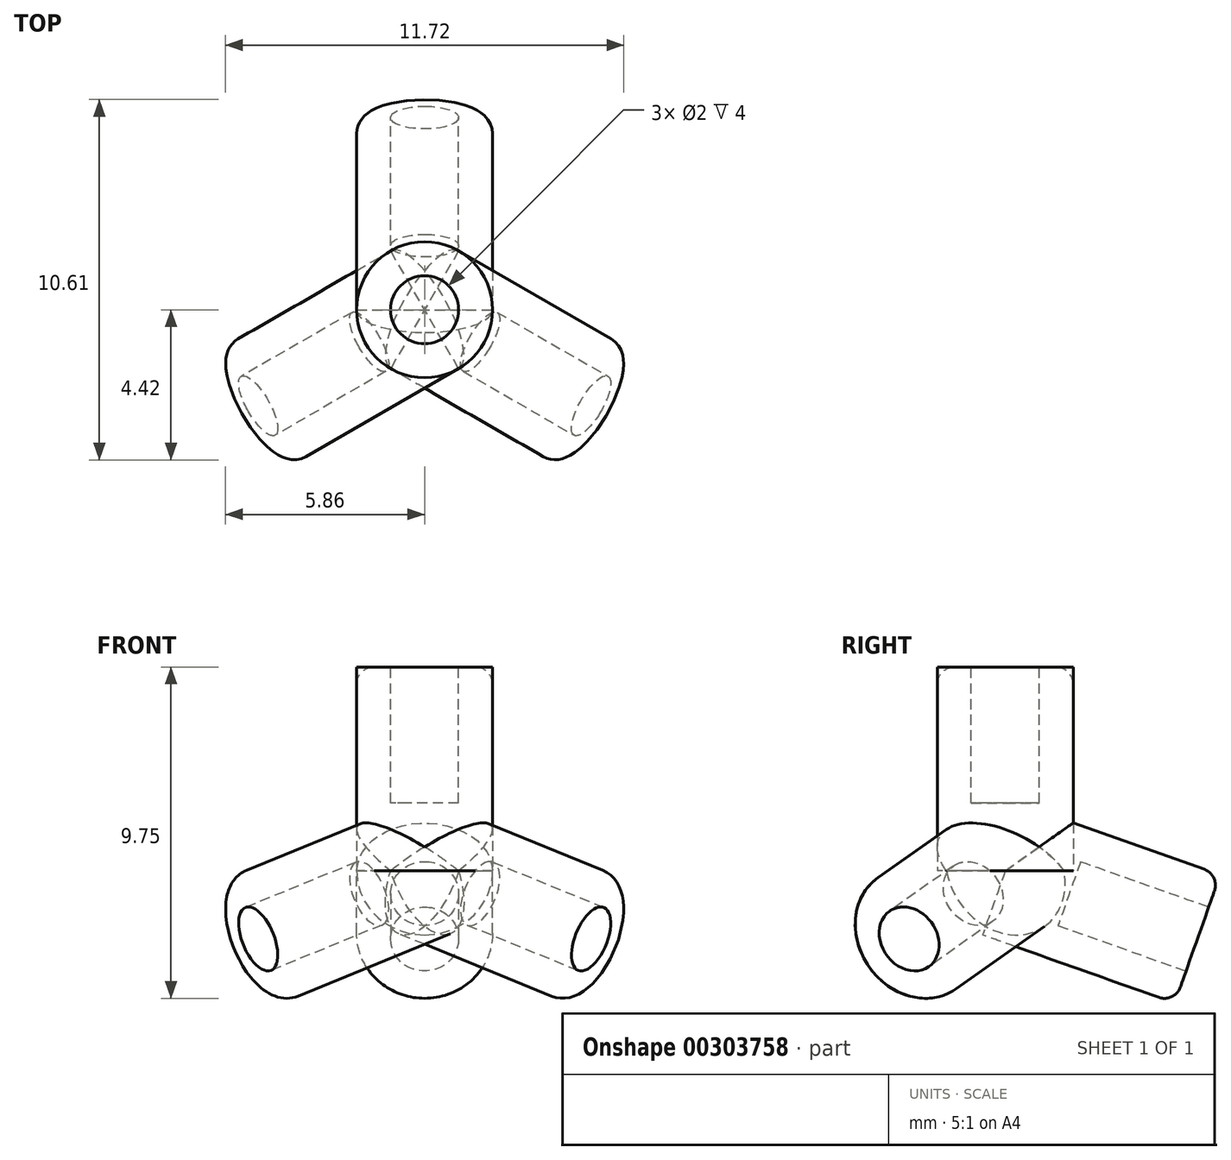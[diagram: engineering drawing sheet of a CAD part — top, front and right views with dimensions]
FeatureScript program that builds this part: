
annotation { "Feature Type Name" : "Feature", "Feature Type Description" : "" }
export const myFeature = defineFeature(function(context is Context, id is Id, definition is map)
    precondition{}
    {
        {
            var Q0;
            Q0=qCreatedBy(makeId("Top.planeOp"),FACE);
            var sketch = newSketch(context, id + "F0", { "sketchPlane" : qUnion([Q0])});
            skCircle(sketch, "E0", {"center": v(0, 0) * mm, "radius": 2 * mm});
            skSolve(sketch);
        }
        {
            var Q0;
            Q0=makeQuery(id+"F0.imprint","IMPRINT",FACE,{"disambiguationData":[TD([[makeQuery(id+"F0.imprint","IMPRINT",EDGE,{"derivedFrom":sQuery(id+"F0.wireOp",EDGE,"E0")}),1.0]])]});
            extrude(context, id + "F1", {"entities" : qUnion([Q0]), "flatOperationType" : FlatOperationType.REMOVE, "offsetDistance" : 25 * mm, "depth" : 6 * mm, "domain" : OperationDomain.MODEL});
        }
        {
            var Q0;
            Q0=qCreatedBy(makeId("Top.planeOp"),FACE);
            var sketch = newSketch(context, id + "F2", { "sketchPlane" : qUnion([Q0])});
            skLineSegment(sketch, "E1", {"start": v(74.45, 0) * mm, "end": v(-75.52, 0) * mm, "construction": true});
            skSolve(sketch);
        }
        {
            var Q0;
            Q0=sQuery(id+"F2.wireOp",EDGE,"E1");
            var Q1;
            Q1=qCreatedBy(makeId("Top.planeOp"),FACE);
            cPlane(context, id + "F3", {"entities" : qUnion([Q0, Q1]), "cplaneType" : CPlaneType.LINE_ANGLE, "offset" : 25 * mm, "angle" : 109.5 * degree, "width" : 150 * mm, "height" : 150 * mm});
        }
        {
            var Q0;
            Q0=qCreatedBy(id+"F3.planeOp",FACE);
            var sketch = newSketch(context, id + "F4", { "sketchPlane" : qUnion([Q0])});
            skCircle(sketch, "E2", {"center": v(0, 0) * mm, "radius": 2 * mm});
            skSolve(sketch);
        }
        {
            var Q0;
            Q0 = qSketchRegion(id + "F4", true);
            extrude(context, id + "F5", {"entities" : qUnion([Q0]), "operationType" : NewBodyOperationType.ADD, "oppositeDirection" : true, "depth" : 6 * mm});
        }
        {
            var Q0;
            Q0=makeQuery(id+"F1.opExtrude","CAP_FACE",FACE,{"disambiguationData":[OSD([sQuery(id+"F0.wireOp",EDGE,"E0")])],"isStart":false});
            var sketch = newSketch(context, id + "F6", { "sketchPlane" : qUnion([Q0])});
            skCircle(sketch, "E3", {"center": v(0, 0) * mm, "radius": 1 * mm});
            skSolve(sketch);
        }
        {
            var Q0;
            Q0=qCreatedBy(makeId("Front.planeOp"),FACE);
            var sketch = newSketch(context, id + "F7", { "sketchPlane" : qUnion([Q0])});
            skLineSegment(sketch, "E4", {"start": v(0, 0) * mm, "end": v(0, 47.07) * mm, "construction": true});
            skSolve(sketch);
        }
        {
            var Q0;
            Q0=makeQuery(id+"F5.opExtrude","CAP_FACE",FACE,{"disambiguationData":[OSD([sQuery(id+"F4.wireOp",EDGE,"E2")])],"isStart":false});
            var sketch = newSketch(context, id + "F8", { "sketchPlane" : qUnion([Q0])});
            skCircle(sketch, "E5", {"center": v(0, 0) * mm, "radius": 1 * mm});
            skSolve(sketch);
        }
        {
            var Q0;
            Q0 = qSketchRegion(id + "F6", true);
            extrude(context, id + "F9", {"entities" : qUnion([Q0]), "operationType" : NewBodyOperationType.REMOVE, "oppositeDirection" : true, "depth" : 4 * mm});
        }
        {
            var Q0;
            Q0=makeQuery(id+"F8.imprint","IMPRINT",FACE,{"disambiguationData":[TD([[makeQuery(id+"F8.imprint","IMPRINT",EDGE,{"derivedFrom":sQuery(id+"F8.wireOp",EDGE,"E5")}),1.0]])]});
            extrude(context, id + "F10", {"entities" : qUnion([Q0]), "operationType" : NewBodyOperationType.REMOVE, "oppositeDirection" : true, "depth" : 4 * mm});
        }
        {
            var Q0;
            Q0=makeQuery(id+"F1.opExtrude","SWEPT_BODY",BODY,{"disambiguationData":[OSD([sQuery(id+"F0.wireOp",EDGE,"E0")])]});
            var Q1;
            Q1=sQuery(id+"F7.wireOp",EDGE,"E4");
            circularPattern(context, id + "F11", {"entities" : qUnion([Q0]), "axis" : qUnion([Q1]), "angle" : 360 * degree, "instanceCount" : 3, "equalSpace" : true});
        }
        {
            var Q0;
            Q0=makeQuery(id+"F1.opExtrude","CAP_EDGE",EDGE,{"disambiguationData":[OSD([sQuery(id+"F0.wireOp",EDGE,"E0")])],"isStart":false});
            var Q1;
            Q1=makeQuery(id+"F11.opPattern","COPY",EDGE,{"derivedFrom":makeQuery(id+"F5.opExtrude","CAP_EDGE",EDGE,{"disambiguationData":[OSD([sQuery(id+"F4.wireOp",EDGE,"E2")])],"isStart":false}),"instanceName":"2"});
            var Q2;
            Q2=makeQuery(id+"F5.opExtrude","CAP_EDGE",EDGE,{"disambiguationData":[OSD([sQuery(id+"F4.wireOp",EDGE,"E2")])],"isStart":false});
            var Q3;
            Q3=makeQuery(id+"F11.opPattern","COPY",EDGE,{"derivedFrom":makeQuery(id+"F5.opExtrude","CAP_EDGE",EDGE,{"disambiguationData":[OSD([sQuery(id+"F4.wireOp",EDGE,"E2")])],"isStart":false}),"instanceName":"1"});
            fillet(context, id + "F12", {"entities" : qUnion([Q0, Q1, Q2, Q3]), "radius" : 0.5 * mm, "tangentPropagation" : true, "allowEdgeOverflow" : false});
        }
    });
